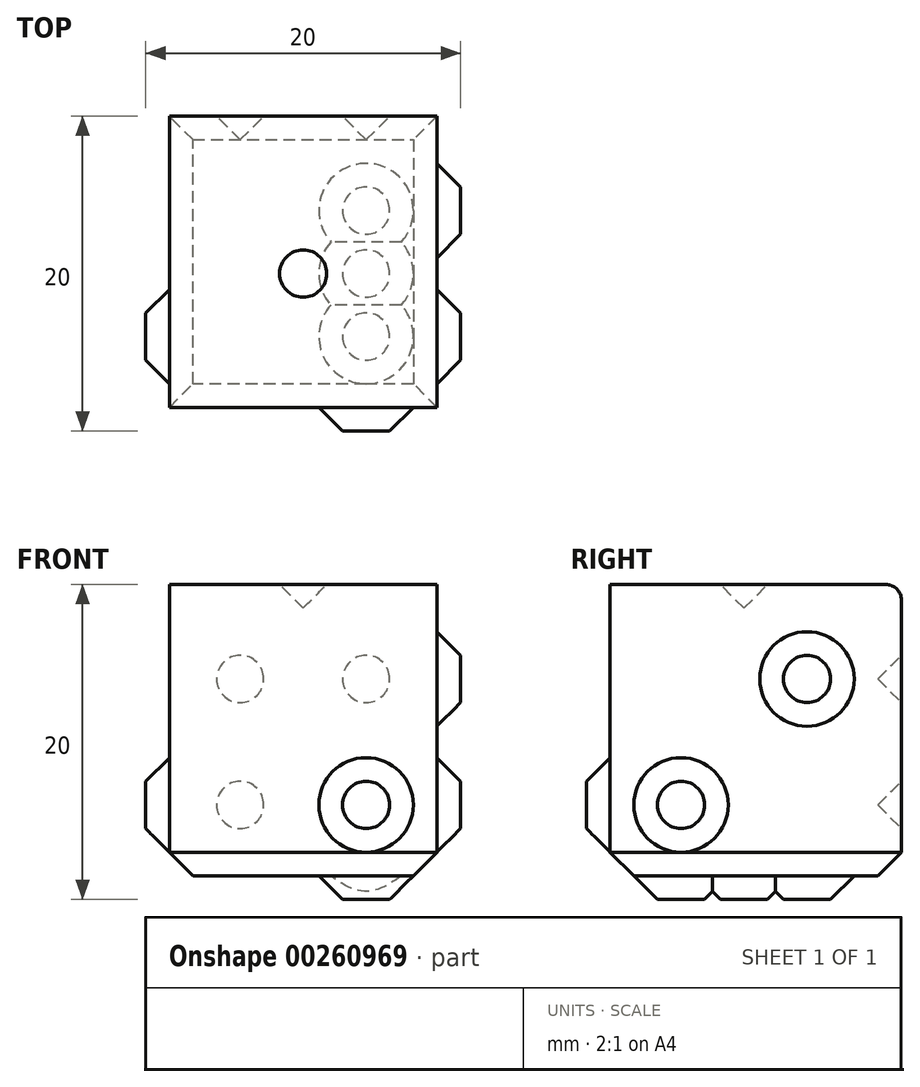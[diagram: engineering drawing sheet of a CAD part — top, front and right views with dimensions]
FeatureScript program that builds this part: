
annotation { "Feature Type Name" : "Feature", "Feature Type Description" : "" }
export const myFeature = defineFeature(function(context is Context, id is Id, definition is map)
    precondition{}
    {
        {
            var Q0;
            Q0=qCreatedBy(makeId("Top.planeOp"),FACE);
            var sketch = newSketch(context, id + "F0", { "sketchPlane" : qUnion([Q0])});
            skLineSegment(sketch, "E0.bottom", {"start": v(0, 0) * mm, "end": v(20, 0) * mm});
            skLineSegment(sketch, "E0.top", {"start": v(0, 20) * mm, "end": v(20, 20) * mm});
            skLineSegment(sketch, "E0.left", {"start": v(0, 0) * mm, "end": v(0, 20) * mm});
            skLineSegment(sketch, "E0.right", {"start": v(20, 0) * mm, "end": v(20, 20) * mm});
            skSolve(sketch);
        }
        {
            var Q0;
            Q0 = qSketchRegion(id + "F0", true);
            extrude(context, id + "F1", {"entities" : qUnion([Q0]), "depth" : 20 * mm});
        }
        {
            var Q0;
            Q0=makeQuery(id+"F1.opExtrude","CAP_FACE",FACE,{"disambiguationData":[OSD([sQuery(id+"F0.wireOp",EDGE,"E0.bottom"),sQuery(id+"F0.wireOp",EDGE,"E0.top"),sQuery(id+"F0.wireOp",EDGE,"E0.left"),sQuery(id+"F0.wireOp",EDGE,"E0.right")])],"isStart":false});
            var sketch = newSketch(context, id + "F2", { "sketchPlane" : qUnion([Q0])});
            skLineSegment(sketch, "E1.0", {"start": v(0, 20) * mm, "end": v(20, 20) * mm, "construction": true});
            skLineSegment(sketch, "E1.1", {"start": v(0, 0) * mm, "end": v(20, 0) * mm, "construction": true});
            skPoint(sketch, "E1.2", {"position": v(10, 0) * mm});
            skLineSegment(sketch, "E2", {"start": v(10, 20) * mm, "end": v(10, 0) * mm, "construction": true});
            skCircle(sketch, "E3", {"center": v(10, 10) * mm, "radius": 1.5 * mm});
            skSolve(sketch);
        }
        {
            var Q0;
            Q0=makeQuery(id+"F2.imprint","IMPRINT",FACE,{"disambiguationData":[TD([[makeQuery(id+"F2.imprint","IMPRINT",EDGE,{"derivedFrom":sQuery(id+"F2.wireOp",EDGE,"E3")}),1.0]])]});
            var Q1;
            Q1=sQuery(id+"F2.wireOp",EDGE,"E3");
            extrude(context, id + "F3", {"entities" : qUnion([Q0]), "operationType" : NewBodyOperationType.REMOVE, "surfaceEntities" : qUnion([Q1]), "oppositeDirection" : true, "depth" : 1.5 * mm});
        }
        {
            var Q0;
            Q0=makeQuery(id+"F1.opExtrude","SWEPT_FACE",FACE,{"disambiguationData":[OSD([sQuery(id+"F0.wireOp",EDGE,"E0.top")])]});
            var sketch = newSketch(context, id + "F4", { "sketchPlane" : qUnion([Q0])});
            skPoint(sketch, "E4.0", {"position": v(-10, 0) * mm});
            skLineSegment(sketch, "E5.0", {"start": v(0, 0) * mm, "end": v(-6, 0) * mm, "construction": true});
            skLineSegment(sketch, "E6", {"start": v(-6, 0) * mm, "end": v(-6, 6) * mm, "construction": true});
            skPoint(sketch, "E7.0", {"position": v(-10, 20) * mm});
            skLineSegment(sketch, "E8", {"start": v(-6, 20) * mm, "end": v(-6, 14) * mm, "construction": true});
            skCircle(sketch, "E9", {"center": v(-6, 6) * mm, "radius": 1.5 * mm});
            skCircle(sketch, "E10", {"center": v(-6, 14) * mm, "radius": 1.5 * mm});
            skPoint(sketch, "E11.orphan", {"position": v(-20, 0) * mm});
            skLineSegment(sketch, "E12.0", {"start": v(0, 20) * mm, "end": v(-6, 20) * mm, "construction": true});
            skPoint(sketch, "E13.orphan", {"position": v(-20, 20) * mm});
            skLineSegment(sketch, "E14.0", {"start": v(0, 0) * mm, "end": v(-20, 0) * mm, "construction": true});
            skLineSegment(sketch, "E14.1", {"start": v(0, 20) * mm, "end": v(-20, 20) * mm, "construction": true});
            skLineSegment(sketch, "E15", {"start": v(-10, 0) * mm, "end": v(-10, 20) * mm, "construction": true});
            skCircle(sketch, "E16.MirrorC", {"center": v(-14, 6) * mm, "radius": 1.5 * mm});
            skCircle(sketch, "E17.MirrorC", {"center": v(-14, 14) * mm, "radius": 1.5 * mm});
            skSolve(sketch);
        }
        {
            var Q0;
            Q0 = qSketchRegion(id + "F4", true);
            extrude(context, id + "F5", {"entities" : qUnion([Q0]), "operationType" : NewBodyOperationType.REMOVE, "oppositeDirection" : true, "depth" : 1.5 * mm});
        }
        {
            var Q0;
            Q0=makeQuery(id+"F1.opExtrude","CAP_FACE",FACE,{"disambiguationData":[OSD([sQuery(id+"F0.wireOp",EDGE,"E0.bottom"),sQuery(id+"F0.wireOp",EDGE,"E0.top"),sQuery(id+"F0.wireOp",EDGE,"E0.left"),sQuery(id+"F0.wireOp",EDGE,"E0.right")])],"isStart":true});
            var sketch = newSketch(context, id + "F6", { "sketchPlane" : qUnion([Q0])});
            skLineSegment(sketch, "E18.0", {"start": v(0, 0) * mm, "end": v(6, 0) * mm, "construction": true});
            skLineSegment(sketch, "E19.0", {"start": v(0, -20) * mm, "end": v(20, -20) * mm, "construction": true});
            skLineSegment(sketch, "E20", {"start": v(6, 0) * mm, "end": v(6, -6) * mm, "construction": true});
            skPoint(sketch, "E21.orphan", {"position": v(20, 0) * mm});
            skCircle(sketch, "E22", {"center": v(6, -6) * mm, "radius": 1.5 * mm});
            skCircle(sketch, "E23", {"center": v(6, -14) * mm, "radius": 1.5 * mm});
            skCircle(sketch, "E24", {"center": v(6, -10) * mm, "radius": 1.5 * mm});
            skLineSegment(sketch, "E25.trimOffspring", {"start": v(6, -14) * mm, "end": v(6, -20) * mm, "construction": true});
            skLineSegment(sketch, "E26", {"start": v(6, -6) * mm, "end": v(6, -10) * mm, "construction": true});
            skLineSegment(sketch, "E27", {"start": v(6, -14) * mm, "end": v(6, -10) * mm, "construction": true});
            skLineSegment(sketch, "E28", {"start": v(10, 0) * mm, "end": v(10, -20) * mm, "construction": true});
            skCircle(sketch, "E29.MirrorC", {"center": v(14, -6) * mm, "radius": 1.5 * mm});
            skCircle(sketch, "E30.MirrorC", {"center": v(14, -10) * mm, "radius": 1.5 * mm});
            skCircle(sketch, "E31.MirrorC", {"center": v(14, -14) * mm, "radius": 1.5 * mm});
            skSolve(sketch);
        }
        {
            var Q0;
            Q0=makeQuery(id+"F1.opExtrude","SWEPT_FACE",FACE,{"disambiguationData":[OSD([sQuery(id+"F0.wireOp",EDGE,"E0.bottom")])]});
            var sketch = newSketch(context, id + "F7", { "sketchPlane" : qUnion([Q0])});
            skLineSegment(sketch, "E32.0", {"start": v(0, 20) * mm, "end": v(6, 20) * mm, "construction": true});
            skLineSegment(sketch, "E33", {"start": v(6, 20) * mm, "end": v(6, 14) * mm});
            skPoint(sketch, "E34.orphan", {"position": v(20, 20) * mm});
            skCircle(sketch, "E35", {"center": v(6, 14) * mm, "radius": 1.5 * mm});
            skArc(sketch, "E36", {"start": v(11.06, 11.06) * mm, "mid": v(8.94, 11.06) * mm, "end": v(8.94, 8.94) * mm});
            skArc(sketch, "E37.MirrorCS", {"start": v(11.06, 11.06) * mm, "mid": v(11.06, 8.94) * mm, "end": v(8.94, 8.94) * mm});
            skCircle(sketch, "E38.MirrorC", {"center": v(14, 6) * mm, "radius": 1.5 * mm});
            skSolve(sketch);
        }
        {
            var Q0;
            Q0=makeQuery(id+"F1.opExtrude","SWEPT_FACE",FACE,{"disambiguationData":[OSD([sQuery(id+"F0.wireOp",EDGE,"E0.right")])]});
            var sketch = newSketch(context, id + "F8", { "sketchPlane" : qUnion([Q0])});
            skLineSegment(sketch, "E39.0", {"start": v(0, 20) * mm, "end": v(6, 20) * mm, "construction": true});
            skLineSegment(sketch, "E40.0", {"start": v(0, 0) * mm, "end": v(20, 0) * mm, "construction": true});
            skLineSegment(sketch, "E41", {"start": v(6, 20) * mm, "end": v(6, 14) * mm, "construction": true});
            skPoint(sketch, "E42.orphan", {"position": v(20, 20) * mm});
            skCircle(sketch, "E43", {"center": v(6, 14) * mm, "radius": 1.5 * mm});
            skCircle(sketch, "E44.MirrorC", {"center": v(6, 6) * mm, "radius": 1.5 * mm});
            skArc(sketch, "E45", {"start": v(10, 11.5) * mm, "mid": v(8.5, 10) * mm, "end": v(10, 8.5) * mm});
            skLineSegment(sketch, "E46", {"start": v(10, 20) * mm, "end": v(10, 0) * mm, "construction": true});
            skCircle(sketch, "E47.MirrorC", {"center": v(14, 14) * mm, "radius": 1.5 * mm});
            skArc(sketch, "E48.MirrorCS", {"start": v(10, 11.5) * mm, "mid": v(11.5, 10) * mm, "end": v(10, 8.5) * mm});
            skCircle(sketch, "E49.MirrorC", {"center": v(14, 6) * mm, "radius": 1.5 * mm});
            skSolve(sketch);
        }
        {
            var Q0;
            Q0=makeQuery(id+"F7.imprint","IMPRINT",FACE,{"disambiguationData":[TD([[makeQuery(id+"F7.imprint","IMPRINT",EDGE,{"derivedFrom":sQuery(id+"F7.wireOp",EDGE,"E35")}),1.0]])]});
            var Q1;
            Q1=makeQuery(id+"F7.imprint","IMPRINT",FACE,{"disambiguationData":[TD([[makeQuery(id+"F7.imprint","IMPRINT",EDGE,{"derivedFrom":sQuery(id+"F7.wireOp",EDGE,"E36")}),1.0]])]});
            var Q2;
            Q2=makeQuery(id+"F7.imprint","IMPRINT",FACE,{"disambiguationData":[TD([[makeQuery(id+"F7.imprint","IMPRINT",EDGE,{"derivedFrom":sQuery(id+"F7.wireOp",EDGE,"E38.MirrorC")}),-1.0]])]});
            extrude(context, id + "F9", {"entities" : qUnion([Q0, Q1, Q2]), "operationType" : NewBodyOperationType.REMOVE, "oppositeDirection" : true, "depth" : 1.5 * mm});
        }
        {
            var Q0;
            Q0=makeQuery(id+"F8.imprint","IMPRINT",FACE,{"disambiguationData":[TD([[makeQuery(id+"F8.imprint","IMPRINT",EDGE,{"derivedFrom":sQuery(id+"F8.wireOp",EDGE,"E49.MirrorC")}),1.0]])]});
            var Q1;
            Q1=makeQuery(id+"F8.imprint","IMPRINT",FACE,{"disambiguationData":[TD([[makeQuery(id+"F8.imprint","IMPRINT",EDGE,{"derivedFrom":sQuery(id+"F8.wireOp",EDGE,"E45")}),1.0]])]});
            var Q2;
            Q2=makeQuery(id+"F8.imprint","IMPRINT",FACE,{"disambiguationData":[TD([[makeQuery(id+"F8.imprint","IMPRINT",EDGE,{"derivedFrom":sQuery(id+"F8.wireOp",EDGE,"E47.MirrorC")}),-1.0]])]});
            var Q3;
            Q3=makeQuery(id+"F8.imprint","IMPRINT",FACE,{"disambiguationData":[TD([[makeQuery(id+"F8.imprint","IMPRINT",EDGE,{"derivedFrom":sQuery(id+"F8.wireOp",EDGE,"E43")}),1.0]])]});
            var Q4;
            Q4=makeQuery(id+"F8.imprint","IMPRINT",FACE,{"disambiguationData":[TD([[makeQuery(id+"F8.imprint","IMPRINT",EDGE,{"derivedFrom":sQuery(id+"F8.wireOp",EDGE,"E44.MirrorC")}),-1.0]])]});
            extrude(context, id + "F10", {"entities" : qUnion([Q0, Q1, Q2, Q3, Q4]), "operationType" : NewBodyOperationType.REMOVE, "oppositeDirection" : true, "depth" : 1.5 * mm});
        }
        {
            var Q0;
            Q0=makeQuery(id+"F6.imprint","IMPRINT",FACE,{"disambiguationData":[TD([[makeQuery(id+"F6.imprint","IMPRINT",EDGE,{"derivedFrom":sQuery(id+"F6.wireOp",EDGE,"E31.MirrorC")}),-1.0]])]});
            var Q1;
            Q1=makeQuery(id+"F6.imprint","IMPRINT",FACE,{"disambiguationData":[TD([[makeQuery(id+"F6.imprint","IMPRINT",EDGE,{"derivedFrom":sQuery(id+"F6.wireOp",EDGE,"E30.MirrorC")}),-1.0]])]});
            var Q2;
            Q2=makeQuery(id+"F6.imprint","IMPRINT",FACE,{"disambiguationData":[TD([[makeQuery(id+"F6.imprint","IMPRINT",EDGE,{"derivedFrom":sQuery(id+"F6.wireOp",EDGE,"E29.MirrorC")}),-1.0]])]});
            var Q3;
            Q3=makeQuery(id+"F6.imprint","IMPRINT",FACE,{"disambiguationData":[TD([[makeQuery(id+"F6.imprint","IMPRINT",EDGE,{"derivedFrom":sQuery(id+"F6.wireOp",EDGE,"E23")}),1.0]])]});
            var Q4;
            Q4=makeQuery(id+"F6.imprint","IMPRINT",FACE,{"disambiguationData":[TD([[makeQuery(id+"F6.imprint","IMPRINT",EDGE,{"derivedFrom":sQuery(id+"F6.wireOp",EDGE,"E24")}),1.0]])]});
            var Q5;
            Q5=makeQuery(id+"F6.imprint","IMPRINT",FACE,{"disambiguationData":[TD([[makeQuery(id+"F6.imprint","IMPRINT",EDGE,{"derivedFrom":sQuery(id+"F6.wireOp",EDGE,"E22")}),1.0]])]});
            extrude(context, id + "F11", {"entities" : qUnion([Q0, Q1, Q2, Q3, Q4, Q5]), "operationType" : NewBodyOperationType.REMOVE, "oppositeDirection" : true, "depth" : 1.5 * mm});
        }
        {
            var Q0;
            Q0=makeQuery(id+"F1.opExtrude","SWEPT_FACE",FACE,{"disambiguationData":[OSD([sQuery(id+"F0.wireOp",EDGE,"E0.left")])]});
            var sketch = newSketch(context, id + "F12", { "sketchPlane" : qUnion([Q0])});
            skLineSegment(sketch, "E50.0", {"start": v(-14, 20) * mm, "end": v(-20, 20) * mm, "construction": true});
            skLineSegment(sketch, "E51.0", {"start": v(0, 0) * mm, "end": v(-20, 0) * mm, "construction": true});
            skLineSegment(sketch, "E52", {"start": v(-14, 20) * mm, "end": v(-14, 14) * mm, "construction": true});
            skPoint(sketch, "E53.orphan", {"position": v(0, 20) * mm});
            skLineSegment(sketch, "E54", {"start": v(-20, 0) * mm, "end": v(0, 20) * mm, "construction": true});
            skCircle(sketch, "E55", {"center": v(-14, 14) * mm, "radius": 1.5 * mm});
            skCircle(sketch, "E56.MirrorC", {"center": v(-6, 6) * mm, "radius": 1.5 * mm});
            skSolve(sketch);
        }
        {
            var Q0;
            Q0=makeQuery(id+"F12.imprint","IMPRINT",FACE,{"disambiguationData":[TD([[makeQuery(id+"F12.imprint","IMPRINT",EDGE,{"derivedFrom":sQuery(id+"F12.wireOp",EDGE,"E55")}),1.0]])]});
            var Q1;
            Q1=makeQuery(id+"F12.imprint","IMPRINT",FACE,{"disambiguationData":[TD([[makeQuery(id+"F12.imprint","IMPRINT",EDGE,{"derivedFrom":sQuery(id+"F12.wireOp",EDGE,"E56.MirrorC")}),-1.0]])]});
            extrude(context, id + "F13", {"entities" : qUnion([Q0, Q1]), "operationType" : NewBodyOperationType.REMOVE, "oppositeDirection" : true, "depth" : 1.5 * mm});
        }
        {
            var Q0;
            Q0=makeQuery(id+"F3.boolean.opBoolean","COPY",EDGE,{"derivedFrom":makeQuery(id+"F3.opExtrude","CAP_EDGE",EDGE,{"disambiguationData":[OSD([sQuery(id+"F2.wireOp",EDGE,"E3")])],"isStart":false})});
            var Q1;
            Q1=makeQuery(id+"F5.boolean.opBoolean","COPY",EDGE,{"derivedFrom":makeQuery(id+"F5.opExtrude","CAP_EDGE",EDGE,{"disambiguationData":[OSD([sQuery(id+"F4.wireOp",EDGE,"E17.MirrorC")])],"isStart":false})});
            var Q2;
            Q2=makeQuery(id+"F5.boolean.opBoolean","COPY",EDGE,{"derivedFrom":makeQuery(id+"F5.opExtrude","CAP_EDGE",EDGE,{"disambiguationData":[OSD([sQuery(id+"F4.wireOp",EDGE,"E16.MirrorC")])],"isStart":false})});
            var Q3;
            Q3=makeQuery(id+"F5.boolean.opBoolean","COPY",EDGE,{"derivedFrom":makeQuery(id+"F5.opExtrude","CAP_EDGE",EDGE,{"disambiguationData":[OSD([sQuery(id+"F4.wireOp",EDGE,"E9")])],"isStart":false})});
            var Q4;
            Q4=makeQuery(id+"F5.boolean.opBoolean","COPY",EDGE,{"derivedFrom":makeQuery(id+"F5.opExtrude","CAP_EDGE",EDGE,{"disambiguationData":[OSD([sQuery(id+"F4.wireOp",EDGE,"E10")])],"isStart":false})});
            var Q5;
            Q5=makeQuery(id+"F9.boolean.opBoolean","COPY",EDGE,{"derivedFrom":makeQuery(id+"F9.opExtrude","CAP_EDGE",EDGE,{"disambiguationData":[OSD([sQuery(id+"F7.wireOp",EDGE,"E35")])],"isStart":false})});
            var Q6;
            Q6=makeQuery(id+"F9.boolean.opBoolean","COPY",EDGE,{"derivedFrom":makeQuery(id+"F9.opExtrude","CAP_EDGE",EDGE,{"disambiguationData":[OSD([sQuery(id+"F7.wireOp",EDGE,"E36"),sQuery(id+"F7.wireOp",EDGE,"E37.MirrorCS")])],"isStart":false})});
            var Q7;
            Q7=makeQuery(id+"F9.boolean.opBoolean","COPY",EDGE,{"derivedFrom":makeQuery(id+"F9.opExtrude","CAP_EDGE",EDGE,{"disambiguationData":[OSD([sQuery(id+"F7.wireOp",EDGE,"E38.MirrorC")])],"isStart":false})});
            var Q8;
            Q8=makeQuery(id+"F11.boolean.opBoolean","COPY",FACE,{"derivedFrom":makeQuery(id+"F11.opExtrude","CAP_FACE",FACE,{"disambiguationData":[OSD([sQuery(id+"F6.wireOp",EDGE,"E22")])],"isStart":false})});
            var Q9;
            Q9=makeQuery(id+"F11.boolean.opBoolean","COPY",EDGE,{"derivedFrom":makeQuery(id+"F11.opExtrude","CAP_EDGE",EDGE,{"disambiguationData":[OSD([sQuery(id+"F6.wireOp",EDGE,"E24")])],"isStart":false})});
            var Q10;
            Q10=makeQuery(id+"F11.boolean.opBoolean","COPY",EDGE,{"derivedFrom":makeQuery(id+"F11.opExtrude","CAP_EDGE",EDGE,{"disambiguationData":[OSD([sQuery(id+"F6.wireOp",EDGE,"E29.MirrorC")])],"isStart":false})});
            var Q11;
            Q11=makeQuery(id+"F11.boolean.opBoolean","COPY",EDGE,{"derivedFrom":makeQuery(id+"F11.opExtrude","CAP_EDGE",EDGE,{"disambiguationData":[OSD([sQuery(id+"F6.wireOp",EDGE,"E30.MirrorC")])],"isStart":false})});
            var Q12;
            Q12=makeQuery(id+"F11.boolean.opBoolean","COPY",FACE,{"derivedFrom":makeQuery(id+"F11.opExtrude","CAP_FACE",FACE,{"disambiguationData":[OSD([sQuery(id+"F6.wireOp",EDGE,"E31.MirrorC")])],"isStart":false})});
            var Q13;
            Q13=makeQuery(id+"F11.boolean.opBoolean","COPY",FACE,{"derivedFrom":makeQuery(id+"F11.opExtrude","CAP_FACE",FACE,{"disambiguationData":[OSD([sQuery(id+"F6.wireOp",EDGE,"E23")])],"isStart":false})});
            var Q14;
            Q14=makeQuery(id+"F10.boolean.opBoolean","COPY",EDGE,{"derivedFrom":makeQuery(id+"F10.opExtrude","CAP_EDGE",EDGE,{"disambiguationData":[OSD([sQuery(id+"F8.wireOp",EDGE,"E43")])],"isStart":false})});
            var Q15;
            Q15=makeQuery(id+"F10.boolean.opBoolean","COPY",EDGE,{"derivedFrom":makeQuery(id+"F10.opExtrude","CAP_EDGE",EDGE,{"disambiguationData":[OSD([sQuery(id+"F8.wireOp",EDGE,"E47.MirrorC")])],"isStart":false})});
            var Q16;
            Q16=makeQuery(id+"F10.boolean.opBoolean","COPY",EDGE,{"derivedFrom":makeQuery(id+"F10.opExtrude","CAP_EDGE",EDGE,{"disambiguationData":[OSD([sQuery(id+"F8.wireOp",EDGE,"E45"),sQuery(id+"F8.wireOp",EDGE,"E48.MirrorCS")])],"isStart":false})});
            var Q17;
            Q17=makeQuery(id+"F10.boolean.opBoolean","COPY",EDGE,{"derivedFrom":makeQuery(id+"F10.opExtrude","CAP_EDGE",EDGE,{"disambiguationData":[OSD([sQuery(id+"F8.wireOp",EDGE,"E44.MirrorC")])],"isStart":false})});
            var Q18;
            Q18=makeQuery(id+"F10.boolean.opBoolean","COPY",EDGE,{"derivedFrom":makeQuery(id+"F10.opExtrude","CAP_EDGE",EDGE,{"disambiguationData":[OSD([sQuery(id+"F8.wireOp",EDGE,"E49.MirrorC")])],"isStart":false})});
            var Q19;
            Q19=makeQuery(id+"F13.boolean.opBoolean","COPY",EDGE,{"derivedFrom":makeQuery(id+"F13.opExtrude","CAP_EDGE",EDGE,{"disambiguationData":[OSD([sQuery(id+"F12.wireOp",EDGE,"E56.MirrorC")])],"isStart":false})});
            var Q20;
            Q20=makeQuery(id+"F13.boolean.opBoolean","COPY",EDGE,{"derivedFrom":makeQuery(id+"F13.opExtrude","CAP_EDGE",EDGE,{"disambiguationData":[OSD([sQuery(id+"F12.wireOp",EDGE,"E55")])],"isStart":false})});
            chamfer(context, id + "F14", {"entities" : qUnion([Q0, Q1, Q2, Q3, Q4, Q5, Q6, Q7, Q8, Q9, Q10, Q11, Q12, Q13, Q14, Q15, Q16, Q17, Q18, Q19, Q20]), "width" : 1.5 * mm, "tangentPropagation" : true});
        }
        {
            var Q0;
            Q0=makeQuery(id+"F1.opExtrude","SWEPT_EDGE",EDGE,{"disambiguationData":[OSD([sQuery(id+"F0.wireOp",EDGE,"E0.top"),sQuery(id+"F0.wireOp",EDGE,"E0.left")])]});
            var Q1;
            Q1=makeQuery(id+"F1.opExtrude","CAP_EDGE",EDGE,{"disambiguationData":[OSD([sQuery(id+"F0.wireOp",EDGE,"E0.left")])],"isStart":false});
            var Q2;
            Q2=makeQuery(id+"F1.opExtrude","CAP_EDGE",EDGE,{"disambiguationData":[OSD([sQuery(id+"F0.wireOp",EDGE,"E0.top")])],"isStart":false});
            var Q3;
            Q3=makeQuery(id+"F1.opExtrude","CAP_EDGE",EDGE,{"disambiguationData":[OSD([sQuery(id+"F0.wireOp",EDGE,"E0.right")])],"isStart":false});
            var Q4;
            Q4=makeQuery(id+"F1.opExtrude","CAP_EDGE",EDGE,{"disambiguationData":[OSD([sQuery(id+"F0.wireOp",EDGE,"E0.bottom")])],"isStart":false});
            var Q5;
            Q5=makeQuery(id+"F1.opExtrude","SWEPT_EDGE",EDGE,{"disambiguationData":[OSD([sQuery(id+"F0.wireOp",EDGE,"E0.bottom"),sQuery(id+"F0.wireOp",EDGE,"E0.left")])]});
            var Q6;
            Q6=makeQuery(id+"F1.opExtrude","SWEPT_EDGE",EDGE,{"disambiguationData":[OSD([sQuery(id+"F0.wireOp",EDGE,"E0.bottom"),sQuery(id+"F0.wireOp",EDGE,"E0.right")])]});
            var Q7;
            Q7=makeQuery(id+"F1.opExtrude","CAP_EDGE",EDGE,{"disambiguationData":[OSD([sQuery(id+"F0.wireOp",EDGE,"E0.bottom")])],"isStart":true});
            var Q8;
            Q8=makeQuery(id+"F1.opExtrude","CAP_EDGE",EDGE,{"disambiguationData":[OSD([sQuery(id+"F0.wireOp",EDGE,"E0.left")])],"isStart":true});
            var Q9;
            Q9=makeQuery(id+"F1.opExtrude","CAP_EDGE",EDGE,{"disambiguationData":[OSD([sQuery(id+"F0.wireOp",EDGE,"E0.top")])],"isStart":true});
            var Q10;
            Q10=makeQuery(id+"F1.opExtrude","CAP_EDGE",EDGE,{"disambiguationData":[OSD([sQuery(id+"F0.wireOp",EDGE,"E0.right")])],"isStart":true});
            var Q11;
            Q11=makeQuery(id+"F1.opExtrude","SWEPT_EDGE",EDGE,{"disambiguationData":[OSD([sQuery(id+"F0.wireOp",EDGE,"E0.top"),sQuery(id+"F0.wireOp",EDGE,"E0.right")])]});
            fillet(context, id + "F15", {"entities" : qUnion([Q0, Q1, Q2, Q3, Q4, Q5, Q6, Q7, Q8, Q9, Q10, Q11]), "radius" : 1 * mm, "tangentPropagation" : true, "allowEdgeOverflow" : false});
        }
    });
